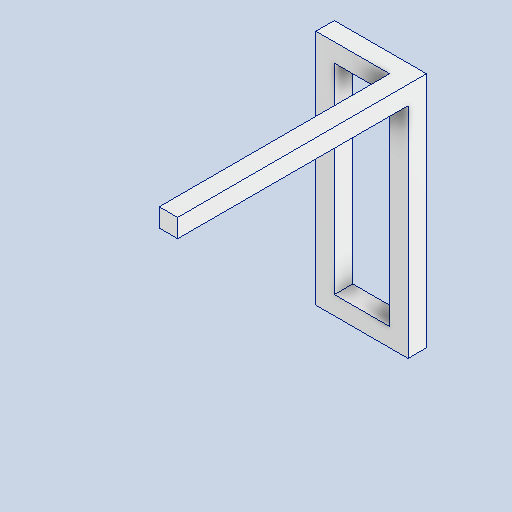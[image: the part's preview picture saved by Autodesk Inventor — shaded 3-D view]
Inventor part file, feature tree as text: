
AUTODESK INVENTOR PART (.ipt)
format: ipt  version: 2025 (Build 290162010, 162A)  size: 151,040 bytes
history: native  units: mm
features: extrude x4, sketch x4, other x4, reference x2, plane x1
ambient origin geometry x8: Origin, YZ Plane, XZ Plane, XY Plane, X Axis, Y Axis, Z Axis, Center Point
bodies: Volumenkörper1 (feature_tree)
feature tree (15):
  extrude  "Extrusion1"  Depth=40.0mm
  extrude  "Extrusion2"  Depth=40.0mm TaperAngle=0.0deg
  extrude  "Extrusion3"  Depth=40.0mm TaperAngle=0.0deg
  plane  "Arbeitsebene1"
  extrude  "Extrusion4"  Depth=500.0mm TaperAngle=0.0deg
  sketch  "Skizze1"  dims[d0=200.0mm d1=40.0mm]
  reference  "Referenz1"
  sketch  "Skizze2"  dims[d2=5.0mm d3=40.0mm d4=0.0mm]
  sketch  "Skizze3"  dims[d5=475.0mm d6=0.0mm d7=40.0mm d8=0.0mm]
  sketch  "Skizze4"  dims[d10=40.0mm d11=500.0mm d12=0.0mm d26=40.0mm d27=0.0mm d9=0.5mm]
  reference  "Referenz2"
  other  "<userpath>\Documents\Inventor\Krandemonstrator\Demonstrator.iam"
  other  "Demonstrator.iam"
  other  "Träger:1"
  other  "Katze_Lagerhalter_vorne:1"
